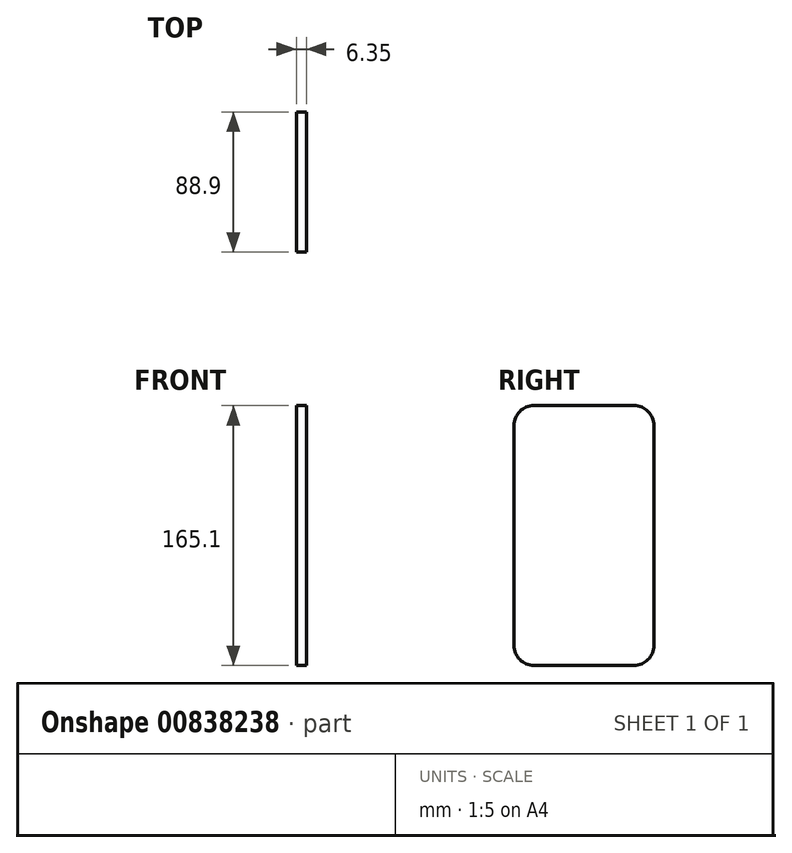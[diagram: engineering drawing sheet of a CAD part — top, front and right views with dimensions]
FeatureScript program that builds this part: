
annotation { "Feature Type Name" : "Feature", "Feature Type Description" : "" }
export const myFeature = defineFeature(function(context is Context, id is Id, definition is map)
    precondition{}
    {
        {
            var Q0;
            Q0=qCreatedBy(makeId("Right.planeOp"),FACE);
            var sketch = newSketch(context, id + "F0", { "sketchPlane" : qUnion([Q0])});
            skLineSegment(sketch, "E0", {"start": v(0, 12.7) * mm, "end": v(0, 152.4) * mm});
            skLineSegment(sketch, "E1", {"start": v(12.7, 165.1) * mm, "end": v(76.2, 165.1) * mm});
            skLineSegment(sketch, "E2", {"start": v(88.9, 152.4) * mm, "end": v(88.9, 12.7) * mm});
            skLineSegment(sketch, "E3", {"start": v(76.2, 0) * mm, "end": v(12.7, 0) * mm});
            skPoint(sketch, "E4.visualSharp", {"position": v(0, 165.1) * mm});
            skArc(sketch, "E4.filletArc", {"start": v(12.7, 165.1) * mm, "mid": v(3.72, 161.38) * mm, "end": v(0, 152.4) * mm});
            skPoint(sketch, "E5.visualSharp", {"position": v(88.9, 165.1) * mm});
            skArc(sketch, "E5.filletArc", {"start": v(88.9, 152.4) * mm, "mid": v(85.18, 161.38) * mm, "end": v(76.2, 165.1) * mm});
            skPoint(sketch, "E6.visualSharp", {"position": v(88.9, 0) * mm});
            skArc(sketch, "E6.filletArc", {"start": v(76.2, 0) * mm, "mid": v(85.18, 3.72) * mm, "end": v(88.9, 12.7) * mm});
            skPoint(sketch, "E7.visualSharp", {"position": v(0, 0) * mm});
            skArc(sketch, "E7.filletArc", {"start": v(0, 12.7) * mm, "mid": v(3.72, 3.72) * mm, "end": v(12.7, 0) * mm});
            skSolve(sketch);
        }
        {
            var Q0;
            Q0=makeQuery(id+"F0.imprint","IMPRINT",FACE,{"disambiguationData":[TD([[makeQuery(id+"F0.imprint","IMPRINT",EDGE,{"derivedFrom":sQuery(id+"F0.wireOp",EDGE,"E0")}),-1.0]])]});
            extrude(context, id + "F1", {"entities" : qUnion([Q0]), "depth" : 6.35 * mm, "offsetDistance" : 25.4 * mm});
        }
    });
